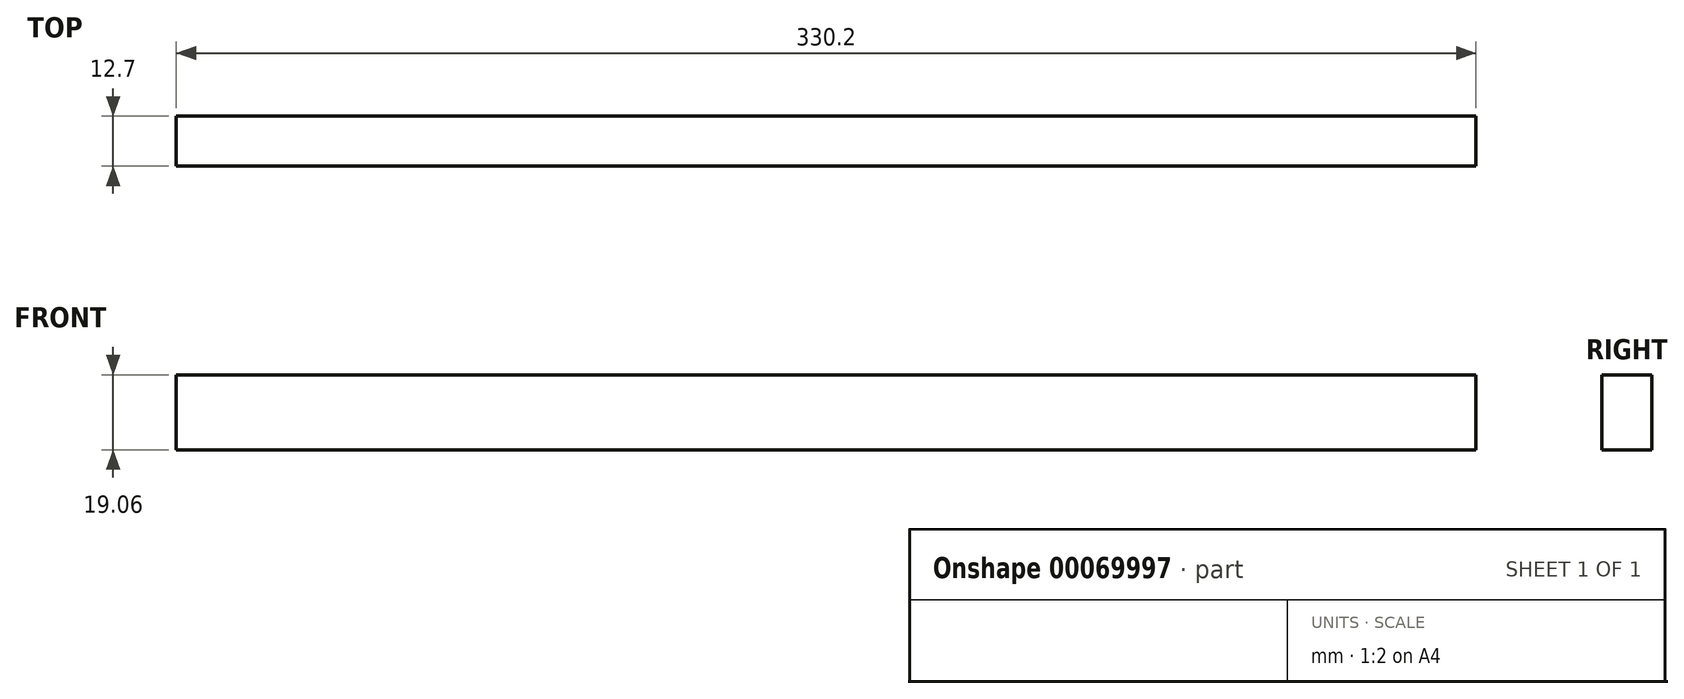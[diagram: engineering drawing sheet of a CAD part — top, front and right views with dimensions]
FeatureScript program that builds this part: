
annotation { "Feature Type Name" : "Feature", "Feature Type Description" : "" }
export const myFeature = defineFeature(function(context is Context, id is Id, definition is map)
    precondition{}
    {
        {
            var Q0;
            Q0=qCreatedBy(makeId("Front.planeOp"),FACE);
            var sketch = newSketch(context, id + "F0", { "sketchPlane" : qUnion([Q0])});
            skLineSegment(sketch, "E0.rect.bottom", {"start": v(165.1, 9.53) * mm, "end": v(-165.1, 9.52) * mm});
            skLineSegment(sketch, "E0.rect.top", {"start": v(165.1, -9.52) * mm, "end": v(-165.1, -9.53) * mm});
            skLineSegment(sketch, "E0.rect.left", {"start": v(165.1, 9.53) * mm, "end": v(165.1, -9.52) * mm});
            skLineSegment(sketch, "E0.rect.right", {"start": v(-165.1, 9.52) * mm, "end": v(-165.1, -9.53) * mm});
            skPoint(sketch, "E0.rect.middle", {"position": v(0, 0) * mm});
            skLineSegment(sketch, "E1", {"start": v(0, 9.52) * mm, "end": v(0, -9.52) * mm, "construction": true});
            skSolve(sketch);
        }
        {
            var Q0;
            Q0=makeQuery(id+"F0.imprint","IMPRINT",FACE,{"disambiguationData":[TD([[makeQuery(id+"F0.imprint","IMPRINT",EDGE,{"derivedFrom":sQuery(id+"F0.wireOp",EDGE,"abd1e121-c28f-4105-937f-708772ba65bf.bottom")}),1.0]])]});
            var Q1;
            {var subQ3=sQuery(id+"F0.wireOp",EDGE,"E0.rect.bottom");Q1=makeQuery(id+"F0.imprint","IMPRINT",FACE,{"disambiguationData":[TD([[makeQuery(id+"F0.imprint","IMPRINT",EDGE,{"derivedFrom":subQ3}),1.0]])]});}
            var Q2;
            Q2=makeQuery(id+"F0.imprint","IMPRINT",FACE,{"disambiguationData":[TD([[makeQuery(id+"F0.imprint","IMPRINT",EDGE,{"derivedFrom":sQuery(id+"F0.wireOp",EDGE,"98e05f21-933e-4f51-9880-0251b27cb64b0.MirrorCS")}),-1.0]])]});
            extrude(context, id + "F1", {"entities" : qUnion([Q0, Q1, Q2]), "depth" : 12.7 * mm});
        }
    });
